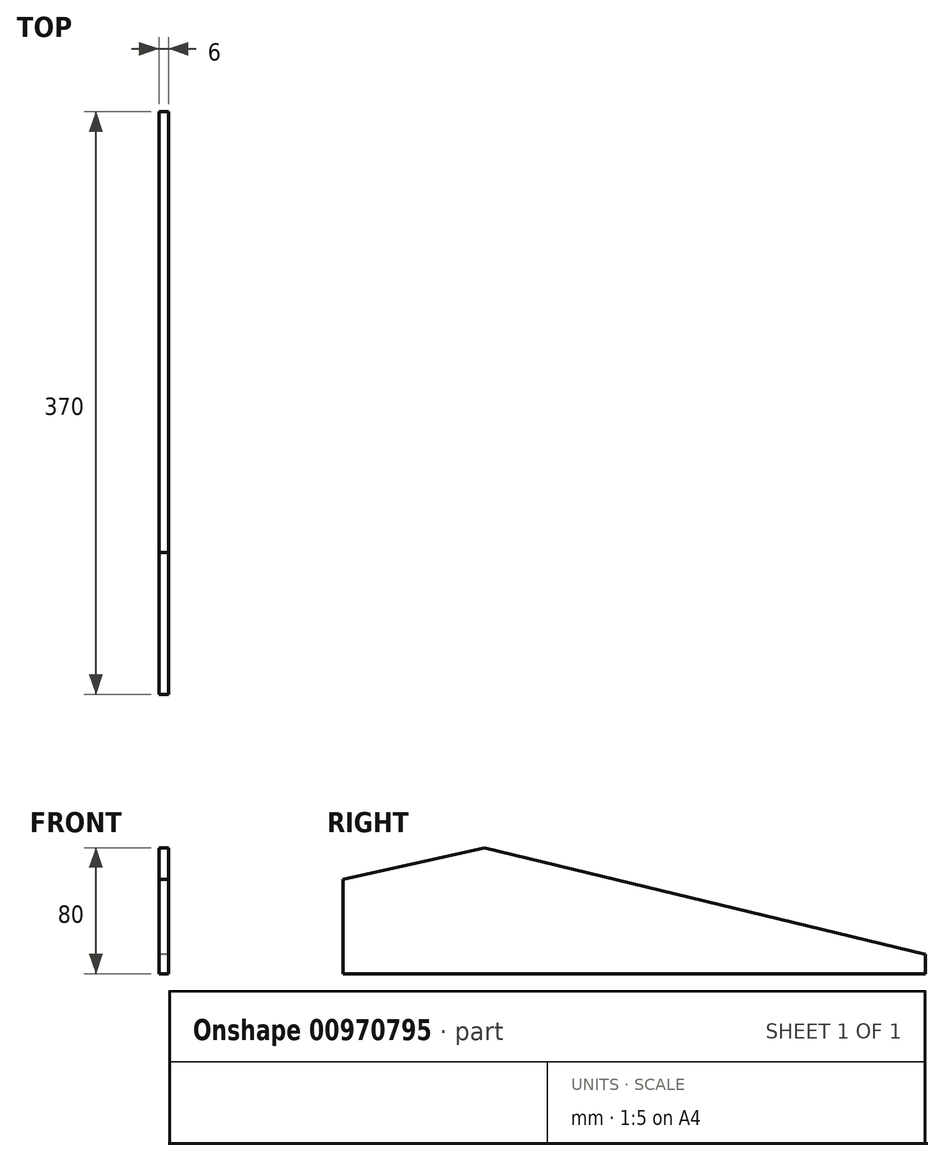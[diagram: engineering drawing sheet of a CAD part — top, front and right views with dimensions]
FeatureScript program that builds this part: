
annotation { "Feature Type Name" : "Feature", "Feature Type Description" : "" }
export const myFeature = defineFeature(function(context is Context, id is Id, definition is map)
    precondition{}
    {
        {
            var Q0;
            Q0=qCreatedBy(makeId("Right.planeOp"),FACE);
            var sketch = newSketch(context, id + "F0", { "sketchPlane" : qUnion([Q0])});
            skLineSegment(sketch, "E0.left", {"start": v(0, 0) * mm, "end": v(0, 60) * mm});
            skLineSegment(sketch, "E0.right", {"start": v(370, 0) * mm, "end": v(370, 12.26) * mm});
            skLineSegment(sketch, "E1", {"start": v(90, 80) * mm, "end": v(-180, 20) * mm});
            skLineSegment(sketch, "E2", {"start": v(-30, 0) * mm, "end": v(400, 0) * mm});
            skLineSegment(sketch, "E3", {"start": v(400, 0) * mm, "end": v(400, 5) * mm});
            skLineSegment(sketch, "E4", {"start": v(90, 80) * mm, "end": v(400, 5) * mm});
            skSolve(sketch);
        }
        {
            var Q0;
            {var subQ1=sQuery(id+"F0.wireOp",EDGE,"E0.left");Q0=makeQuery(id+"F0.imprint","IMPRINT",FACE,{"disambiguationData":[TD([[makeQuery(id+"F0.imprint","IMPRINT",EDGE,{"derivedFrom":subQ1}),-1.0]])]});}
            extrude(context, id + "F1", {"entities" : qUnion([Q0]), "depth" : 6 * mm, "offsetDistance" : 25 * mm});
        }
    });
